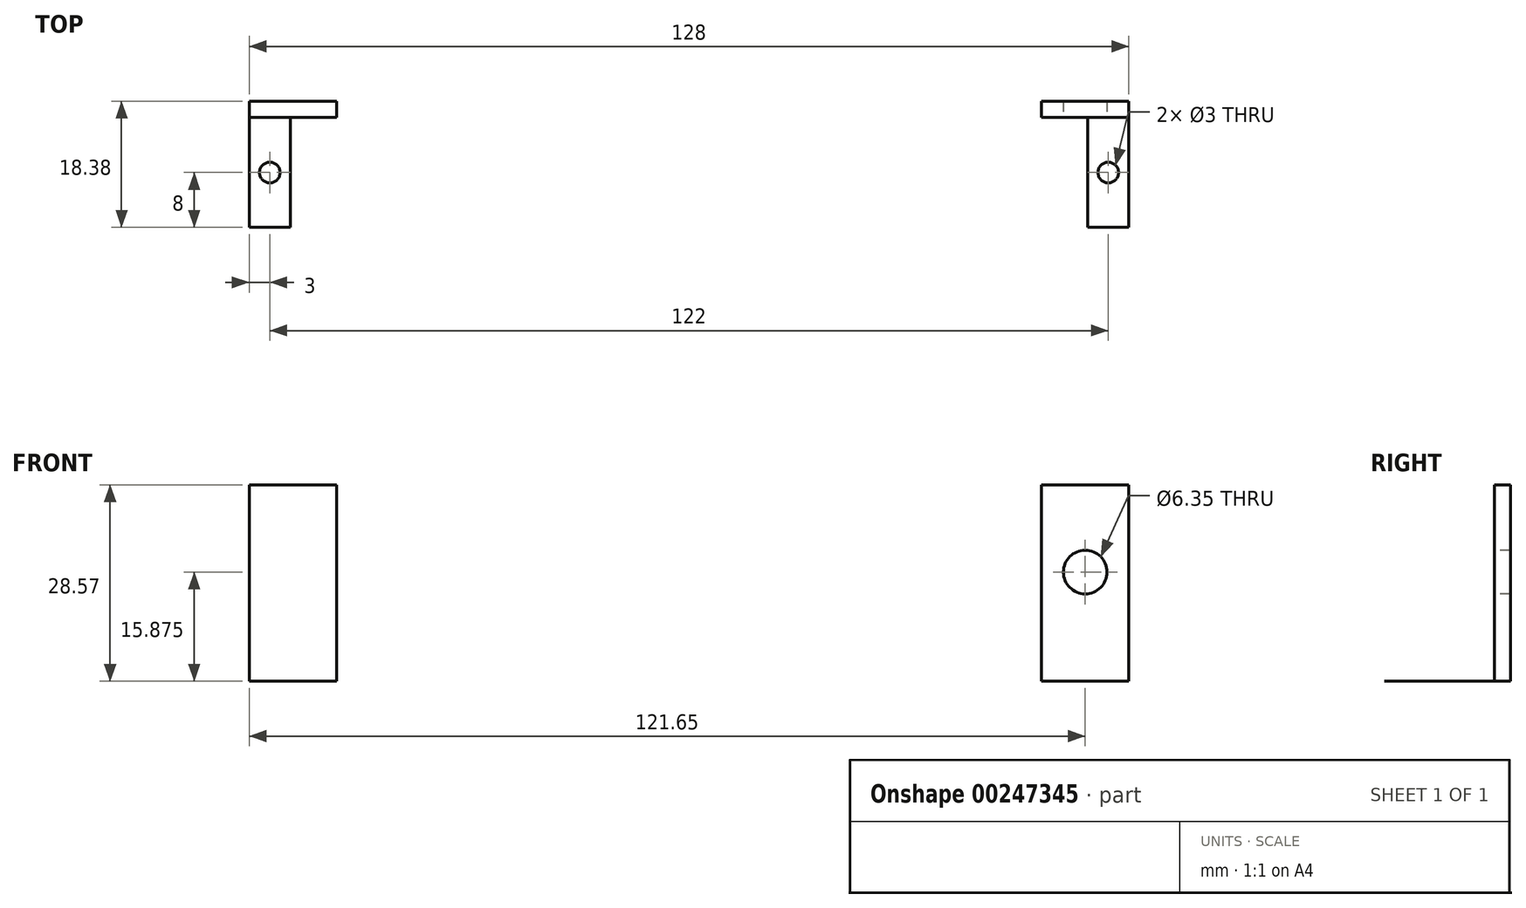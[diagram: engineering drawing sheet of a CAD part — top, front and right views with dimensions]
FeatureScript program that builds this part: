
annotation { "Feature Type Name" : "Feature", "Feature Type Description" : "" }
export const myFeature = defineFeature(function(context is Context, id is Id, definition is map)
    precondition{}
    {
        {
            var Q0;
            Q0=qCreatedBy(makeId("Top.planeOp"),FACE);
            var sketch = newSketch(context, id + "F0", { "sketchPlane" : qUnion([Q0])});
            skLineSegment(sketch, "E0.bottom", {"start": v(-64, -8) * mm, "end": v(64, -8) * mm});
            skLineSegment(sketch, "E0.top", {"start": v(-64, 8) * mm, "end": v(64, 8) * mm});
            skLineSegment(sketch, "E0.left", {"start": v(-64, -8) * mm, "end": v(-64, 8) * mm});
            skLineSegment(sketch, "E0.right", {"start": v(64, -8) * mm, "end": v(64, 8) * mm});
            skPoint(sketch, "E0.middle", {"position": v(0, 0) * mm});
            skLineSegment(sketch, "E1.bottom", {"start": v(-57, -1.42) * mm, "end": v(57, -1.42) * mm});
            skLineSegment(sketch, "E1.top", {"start": v(-57, 1.42) * mm, "end": v(57, 1.42) * mm});
            skLineSegment(sketch, "E1.left", {"start": v(-57, -1.42) * mm, "end": v(-57, 1.42) * mm});
            skLineSegment(sketch, "E1.right", {"start": v(57, -1.42) * mm, "end": v(57, 1.42) * mm});
            skLineSegment(sketch, "E2.bottom", {"start": v(-58, -8) * mm, "end": v(58, -8) * mm});
            skLineSegment(sketch, "E2.top", {"start": v(-58, 8) * mm, "end": v(58, 8) * mm});
            skLineSegment(sketch, "E2.left", {"start": v(-58, -8) * mm, "end": v(-58, 8) * mm});
            skLineSegment(sketch, "E2.right", {"start": v(58, -8) * mm, "end": v(58, 8) * mm});
            skLineSegment(sketch, "E3", {"start": v(-64, 0) * mm, "end": v(-58, 0) * mm, "construction": true});
            skLineSegment(sketch, "E4", {"start": v(58, 0) * mm, "end": v(64, 0) * mm, "construction": true});
            skCircle(sketch, "E5", {"center": v(-61, 0) * mm, "radius": 1.5 * mm});
            skCircle(sketch, "E6", {"center": v(61, 0) * mm, "radius": 1.5 * mm});
            skLineSegment(sketch, "E7", {"start": v(-64, 10.38) * mm, "end": v(64, 10.38) * mm});
            skLineSegment(sketch, "E8", {"start": v(-64, 10.38) * mm, "end": v(-64, 8) * mm});
            skLineSegment(sketch, "E9", {"start": v(64, 10.38) * mm, "end": v(64, 8) * mm});
            skLineSegment(sketch, "E10", {"start": v(-51.3, 10.38) * mm, "end": v(-51.3, 8) * mm});
            skLineSegment(sketch, "E11", {"start": v(0, 10.38) * mm, "end": v(0, -8) * mm, "construction": true});
            skLineSegment(sketch, "E12.MirrorCS", {"start": v(51.3, 10.38) * mm, "end": v(51.3, 8) * mm});
            skSolve(sketch);
        }
        {
            var Q0;
            {var subQ1=sQuery(id+"F0.wireOp",EDGE,"E0.left");Q0=makeQuery(id+"F0.imprint","IMPRINT",FACE,{"disambiguationData":[TD([[makeQuery(id+"F0.imprint","IMPRINT",EDGE,{"derivedFrom":subQ1}),-1.0]])]});}
            var Q1;
            {var subQ1=sQuery(id+"F0.wireOp",EDGE,"E0.right");Q1=makeQuery(id+"F0.imprint","IMPRINT",FACE,{"disambiguationData":[TD([[makeQuery(id+"F0.imprint","IMPRINT",EDGE,{"derivedFrom":subQ1}),1.0]])]});}
            extrude(context, id + "F1", {"entities" : qUnion([Q0, Q1]), "depth" : 1 / 203.2 * mm});
        }
        {
            var Q0;
            {var subQ0=sQuery(id+"F0.wireOp",EDGE,"E9");Q0=makeQuery(id+"F0.imprint","IMPRINT",FACE,{"disambiguationData":[TD([[makeQuery(id+"F0.imprint","IMPRINT",EDGE,{"derivedFrom":subQ0}),-1.0]])]});}
            var Q1;
            {var subQ0=sQuery(id+"F0.wireOp",EDGE,"E8");Q1=makeQuery(id+"F0.imprint","IMPRINT",FACE,{"disambiguationData":[TD([[makeQuery(id+"F0.imprint","IMPRINT",EDGE,{"derivedFrom":subQ0}),1.0]])]});}
            extrude(context, id + "F2", {"entities" : qUnion([Q0, Q1]), "operationType" : NewBodyOperationType.ADD, "depth" : 28.57 * mm});
        }
        {
            var Q0;
            {var subQ0=sQuery(id+"F0.wireOp",EDGE,"E2.top");var subQ1=sQuery(id+"F0.wireOp",EDGE,"E0.top");Q0=makeQuery(id+"F2.opExtrude","SWEPT_FACE",FACE,{"disambiguationData":[OSD([subQ1,subQ0]),TDD([makeQuery(id+"F0.imprint","IMPRINT",EDGE,{"disambiguationData":[TD([[makeQuery(id+"F0.imprint","INTERSECT",VERTEX,{"derivedFrom":[subQ1,sQuery(id+"F0.wireOp",EDGE,"E0.right"),sQuery(id+"F0.wireOp",EDGE,"E9")]}),1.0]])],"derivedFrom":subQ1}),makeQuery(id+"F0.imprint","IMPRINT",EDGE,{"disambiguationData":[TD([[makeQuery(id+"F0.imprint","INTERSECT",VERTEX,{"derivedFrom":[subQ0,sQuery(id+"F0.wireOp",EDGE,"E12.MirrorCS")]}),-1.0]])],"derivedFrom":subQ0})])]});}
            var sketch = newSketch(context, id + "F3", { "sketchPlane" : qUnion([Q0])});
            skLineSegment(sketch, "E13.bottom", {"start": v(64, 28.58) * mm, "end": v(51.3, 28.58) * mm, "construction": true});
            skLineSegment(sketch, "E13.top", {"start": v(64, 0) * mm, "end": v(51.3, 0) * mm, "construction": true});
            skLineSegment(sketch, "E13.left", {"start": v(64, 28.58) * mm, "end": v(64, 0) * mm, "construction": true});
            skLineSegment(sketch, "E13.right", {"start": v(51.3, 28.58) * mm, "end": v(51.3, 0) * mm, "construction": true});
            skCircle(sketch, "E14", {"center": v(57.65, 15.88) * mm, "radius": 3.18 * mm});
            skSolve(sketch);
        }
        {
            var Q0;
            Q0=makeQuery(id+"F3.imprint","IMPRINT",FACE,{"disambiguationData":[TD([[makeQuery(id+"F3.imprint","IMPRINT",EDGE,{"derivedFrom":sQuery(id+"F3.wireOp",EDGE,"E14")}),1.0]])]});
            extrude(context, id + "F4", {"entities" : qUnion([Q0]), "operationType" : NewBodyOperationType.REMOVE, "endBound" : BoundingType.THROUGH_ALL, "oppositeDirection" : true, "depth" : 25.4 * mm});
        }
    });
